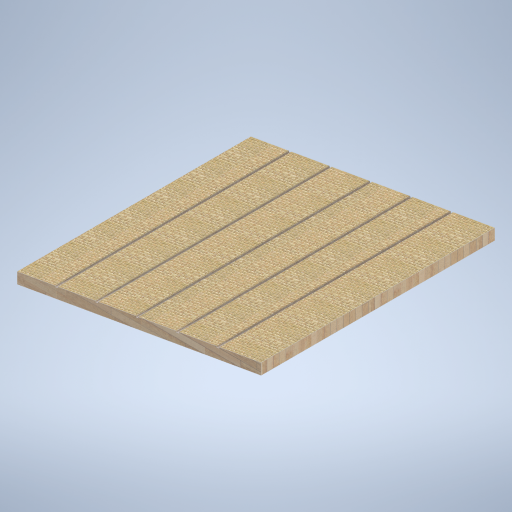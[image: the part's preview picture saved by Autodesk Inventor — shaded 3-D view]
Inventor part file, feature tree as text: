
AUTODESK INVENTOR PART (.ipt)
format: ipt  version: 2024.2 (Build 282272000, 272)  size: 423,936 bytes
history: native  units: mm
features: sketch x4, plane x3, extrude x2
ambient origin geometry x8: Origin, YZ Plane, XZ Plane, XY Plane, X Axis, Y Axis, Z Axis, Center Point
bodies: Solid1 (feature_tree)
feature tree (9):
  sketch  "Sketch1"  dims[d0=100.0mm d1=2108.0mm]
  plane  "Work Plane2"
  sketch  "Sketch2"  dims[d2=2200.0mm d3=13.962634mm]
  plane  "Work Plane3"
  extrude  "Extrusion1"  Depth=2108.0mm
  extrude  "Extrusion2"  Depth=2200.0mm
  plane  "Work Plane1"
  sketch  "Sketch3"  dims[d4=13.962634mm]
  sketch  "Sketch4"  dims[d5=2108.0mm d6=0.0mm d7=350.0mm d8=350.0mm d9=350.0mm d10=350.0mm d11=350.0mm d12=0.0mm d13=0.0mm]
